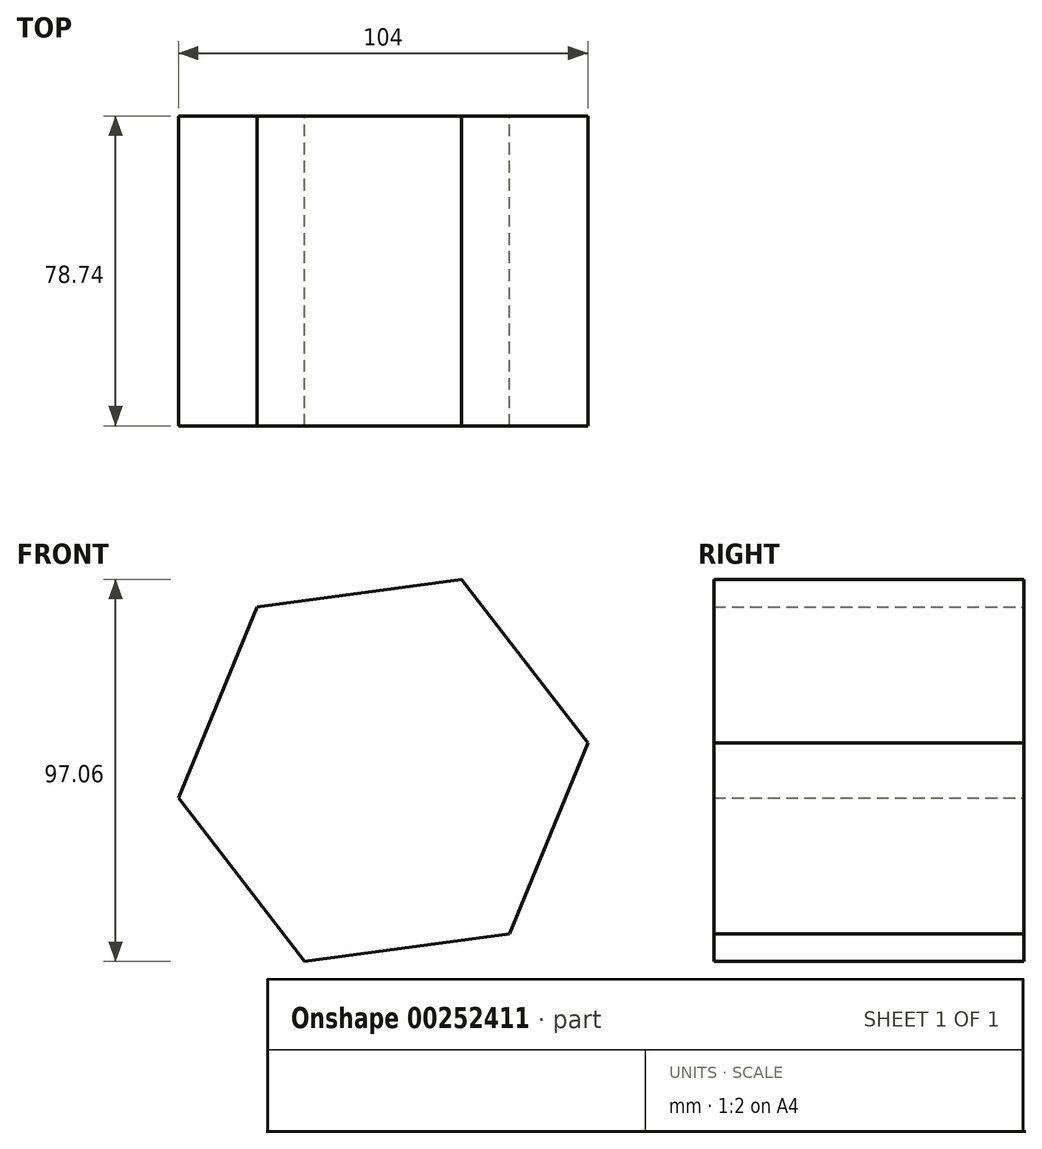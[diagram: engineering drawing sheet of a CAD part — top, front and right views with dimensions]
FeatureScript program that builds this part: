
annotation { "Feature Type Name" : "Feature", "Feature Type Description" : "" }
export const myFeature = defineFeature(function(context is Context, id is Id, definition is map)
    precondition{}
    {
        {
            var Q0;
            Q0=qCreatedBy(makeId("Front.planeOp"),FACE);
            var sketch = newSketch(context, id + "F0", { "sketchPlane" : qUnion([Q0])});
            skCircle(sketch, "E0.cCircle", {"center": v(0, 0) * mm, "radius": 52.47 * mm, "construction": true});
            skLineSegment(sketch, "E0.0", {"start": v(-32.06, 41.54) * mm, "end": v(19.94, 48.53) * mm});
            skLineSegment(sketch, "E0.1", {"start": v(19.94, 48.53) * mm, "end": v(52, 7) * mm});
            skLineSegment(sketch, "E0.2", {"start": v(52, 7) * mm, "end": v(32.06, -41.54) * mm});
            skLineSegment(sketch, "E0.3", {"start": v(32.06, -41.54) * mm, "end": v(-19.94, -48.53) * mm});
            skLineSegment(sketch, "E0.4", {"start": v(-19.94, -48.53) * mm, "end": v(-52, -7) * mm});
            skLineSegment(sketch, "E0.5", {"start": v(-52, -7) * mm, "end": v(-32.06, 41.54) * mm});
            skSolve(sketch);
        }
        {
            var Q0;
            Q0 = qSketchRegion(id + "F0", true);
            extrude(context, id + "F1", {"entities" : qUnion([Q0]), "endBound" : BoundingType.SYMMETRIC, "depth" : 78.74 * mm});
        }
    });
